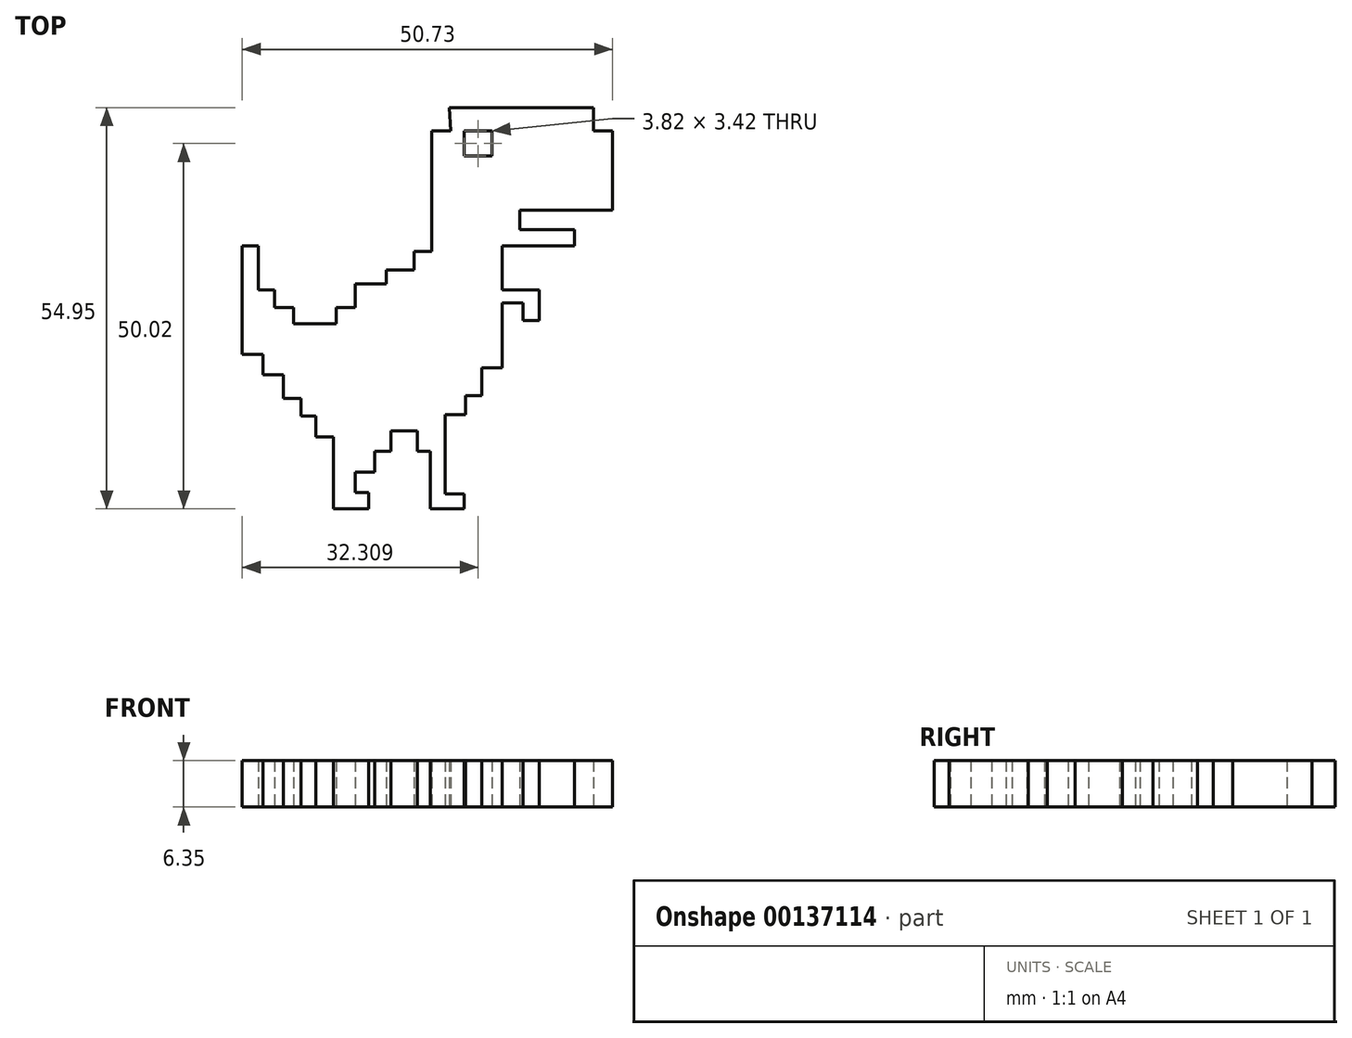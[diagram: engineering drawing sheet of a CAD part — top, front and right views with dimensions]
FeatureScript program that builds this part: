
annotation { "Feature Type Name" : "Feature", "Feature Type Description" : "" }
export const myFeature = defineFeature(function(context is Context, id is Id, definition is map)
    precondition{}
    {
        {
            var Q0;
            Q0=qCreatedBy(makeId("Top.planeOp"),FACE);
            var sketch = newSketch(context, id + "F0", { "sketchPlane" : qUnion([Q0])});
            skLineSegment(sketch, "E0", {"start": v(-19.73, 22.24) * mm, "end": v(0, 22.24) * mm});
            skLineSegment(sketch, "E1", {"start": v(0, 22.24) * mm, "end": v(0, 19.02) * mm});
            skLineSegment(sketch, "E2", {"start": v(0, 19.02) * mm, "end": v(2.62, 19.02) * mm});
            skLineSegment(sketch, "E3", {"start": v(2.62, 19.02) * mm, "end": v(2.62, 8.15) * mm});
            skLineSegment(sketch, "E4", {"start": v(2.62, 8.15) * mm, "end": v(-10.06, 8.15) * mm});
            skLineSegment(sketch, "E5", {"start": v(-10.06, 8.15) * mm, "end": v(-10.06, 5.54) * mm});
            skLineSegment(sketch, "E6", {"start": v(-10.06, 5.54) * mm, "end": v(-2.62, 5.54) * mm});
            skLineSegment(sketch, "E7", {"start": v(-2.62, 5.54) * mm, "end": v(-2.62, 3.32) * mm});
            skLineSegment(sketch, "E8", {"start": v(-2.62, 3.32) * mm, "end": v(-12.48, 3.32) * mm});
            skLineSegment(sketch, "E9", {"start": v(-12.48, 3.32) * mm, "end": v(-12.48, -2.72) * mm});
            skLineSegment(sketch, "E10", {"start": v(-12.48, -2.72) * mm, "end": v(-7.45, -2.72) * mm});
            skLineSegment(sketch, "E11", {"start": v(-7.45, -2.72) * mm, "end": v(-7.45, -6.94) * mm});
            skLineSegment(sketch, "E12", {"start": v(-9.66, -6.94) * mm, "end": v(-9.66, -4.53) * mm});
            skLineSegment(sketch, "E13", {"start": v(-9.66, -4.53) * mm, "end": v(-12.48, -4.53) * mm});
            skLineSegment(sketch, "E14", {"start": v(-12.48, -4.53) * mm, "end": v(-12.48, -13.39) * mm});
            skLineSegment(sketch, "E15", {"start": v(-12.48, -13.39) * mm, "end": v(-15.3, -13.39) * mm});
            skLineSegment(sketch, "E16", {"start": v(-15.3, -13.39) * mm, "end": v(-15.3, -17.2) * mm});
            skLineSegment(sketch, "E17", {"start": v(-15.3, -17.2) * mm, "end": v(-17.51, -17.2) * mm});
            skLineSegment(sketch, "E18", {"start": v(-17.51, -17.2) * mm, "end": v(-17.51, -19.83) * mm});
            skLineSegment(sketch, "E19", {"start": v(-17.51, -19.83) * mm, "end": v(-20.33, -19.83) * mm});
            skLineSegment(sketch, "E20", {"start": v(-20.33, -19.83) * mm, "end": v(-20.33, -30.7) * mm});
            skLineSegment(sketch, "E21", {"start": v(-20.33, -30.7) * mm, "end": v(-17.71, -30.7) * mm});
            skLineSegment(sketch, "E22", {"start": v(-17.71, -30.7) * mm, "end": v(-17.71, -32.7) * mm});
            skLineSegment(sketch, "E23", {"start": v(-17.71, -32.7) * mm, "end": v(-22.34, -32.7) * mm});
            skLineSegment(sketch, "E24", {"start": v(-22.34, -32.7) * mm, "end": v(-22.34, -24.86) * mm});
            skLineSegment(sketch, "E25", {"start": v(-22.34, -24.86) * mm, "end": v(-24.15, -24.86) * mm});
            skLineSegment(sketch, "E26", {"start": v(-24.15, -24.86) * mm, "end": v(-24.15, -22.04) * mm});
            skLineSegment(sketch, "E27", {"start": v(-24.15, -22.04) * mm, "end": v(-27.78, -22.04) * mm});
            skLineSegment(sketch, "E28", {"start": v(-27.78, -22.04) * mm, "end": v(-27.78, -24.86) * mm});
            skLineSegment(sketch, "E29", {"start": v(-27.78, -24.86) * mm, "end": v(-30, -24.86) * mm});
            skLineSegment(sketch, "E30", {"start": v(-30, -24.86) * mm, "end": v(-30, -27.68) * mm});
            skLineSegment(sketch, "E31", {"start": v(-30, -27.68) * mm, "end": v(-32.6, -27.68) * mm});
            skLineSegment(sketch, "E32", {"start": v(-32.6, -27.68) * mm, "end": v(-32.6, -30.5) * mm});
            skLineSegment(sketch, "E33", {"start": v(-32.6, -30.5) * mm, "end": v(-30.8, -30.5) * mm});
            skLineSegment(sketch, "E34", {"start": v(-30.8, -30.5) * mm, "end": v(-30.8, -32.7) * mm});
            skLineSegment(sketch, "E35", {"start": v(-30.8, -32.7) * mm, "end": v(-35.63, -32.7) * mm});
            skLineSegment(sketch, "E36", {"start": v(-35.63, -32.7) * mm, "end": v(-35.63, -22.85) * mm});
            skLineSegment(sketch, "E37", {"start": v(-35.63, -22.85) * mm, "end": v(-38.04, -22.85) * mm});
            skLineSegment(sketch, "E38", {"start": v(-38.04, -22.85) * mm, "end": v(-38.04, -20.03) * mm});
            skLineSegment(sketch, "E39", {"start": v(-38.04, -20.03) * mm, "end": v(-40.06, -20.03) * mm});
            skLineSegment(sketch, "E40", {"start": v(-40.06, -20.03) * mm, "end": v(-40.06, -17.61) * mm});
            skLineSegment(sketch, "E41", {"start": v(-40.06, -17.61) * mm, "end": v(-42.47, -17.61) * mm});
            skLineSegment(sketch, "E42", {"start": v(-42.47, -17.61) * mm, "end": v(-42.47, -14.4) * mm});
            skLineSegment(sketch, "E43", {"start": v(-42.47, -14.4) * mm, "end": v(-45.29, -14.4) * mm});
            skLineSegment(sketch, "E44", {"start": v(-45.29, -14.4) * mm, "end": v(-45.29, -11.57) * mm});
            skLineSegment(sketch, "E45", {"start": v(-45.29, -11.57) * mm, "end": v(-48.1, -11.57) * mm});
            skLineSegment(sketch, "E46", {"start": v(-48.1, -11.57) * mm, "end": v(-48.1, 3.32) * mm});
            skLineSegment(sketch, "E47", {"start": v(-48.1, 3.32) * mm, "end": v(-45.9, 3.32) * mm});
            skLineSegment(sketch, "E48", {"start": v(-45.9, 3.32) * mm, "end": v(-45.9, -2.72) * mm});
            skLineSegment(sketch, "E49", {"start": v(-45.9, -2.72) * mm, "end": v(-43.68, -2.72) * mm});
            skLineSegment(sketch, "E50", {"start": v(-43.68, -2.72) * mm, "end": v(-43.68, -5.13) * mm});
            skLineSegment(sketch, "E51", {"start": v(-43.68, -5.13) * mm, "end": v(-41.06, -5.13) * mm});
            skLineSegment(sketch, "E52", {"start": v(-41.06, -5.13) * mm, "end": v(-41.06, -7.35) * mm});
            skLineSegment(sketch, "E53", {"start": v(-41.06, -7.35) * mm, "end": v(-35.22, -7.35) * mm});
            skLineSegment(sketch, "E54", {"start": v(-35.22, -7.35) * mm, "end": v(-35.22, -5.13) * mm});
            skLineSegment(sketch, "E55", {"start": v(-35.22, -5.13) * mm, "end": v(-32.6, -5.13) * mm});
            skLineSegment(sketch, "E56", {"start": v(-32.6, -5.13) * mm, "end": v(-32.6, -1.91) * mm});
            skLineSegment(sketch, "E57", {"start": v(-32.6, -1.91) * mm, "end": v(-28.38, -1.91) * mm});
            skLineSegment(sketch, "E58", {"start": v(-28.38, -1.91) * mm, "end": v(-28.38, 0) * mm});
            skLineSegment(sketch, "E59", {"start": v(-28.38, 0) * mm, "end": v(-24.56, 0) * mm});
            skLineSegment(sketch, "E60", {"start": v(-24.56, 0) * mm, "end": v(-24.56, 2.52) * mm});
            skLineSegment(sketch, "E61", {"start": v(-24.56, 2.52) * mm, "end": v(-22.14, 2.52) * mm});
            skLineSegment(sketch, "E62", {"start": v(-22.14, 2.52) * mm, "end": v(-22.14, 19.02) * mm});
            skLineSegment(sketch, "E63", {"start": v(-22.14, 19.02) * mm, "end": v(-19.52, 19.02) * mm});
            skLineSegment(sketch, "E64", {"start": v(-19.52, 19.02) * mm, "end": v(-19.73, 22.24) * mm});
            skLineSegment(sketch, "E65.bottom", {"start": v(-17.71, 19.02) * mm, "end": v(-13.89, 19.02) * mm});
            skLineSegment(sketch, "E65.top", {"start": v(-17.71, 15.6) * mm, "end": v(-13.89, 15.6) * mm});
            skLineSegment(sketch, "E65.left", {"start": v(-17.71, 19.02) * mm, "end": v(-17.71, 15.6) * mm});
            skLineSegment(sketch, "E65.right", {"start": v(-13.89, 19.02) * mm, "end": v(-13.89, 15.6) * mm});
            skLineSegment(sketch, "E66", {"start": v(-7.45, -6.94) * mm, "end": v(-9.66, -6.94) * mm});
            skSolve(sketch);
        }
        {
            var Q0;
            Q0=makeQuery(id+"F0.imprint","IMPRINT",FACE,{"disambiguationData":[TD([[makeQuery(id+"F0.imprint","IMPRINT",EDGE,{"derivedFrom":sQuery(id+"F0.wireOp",EDGE,"E0")}),-1.0]])]});
            extrude(context, id + "F1", {"entities" : qUnion([Q0]), "depth" : 6.35 * mm});
        }
    });
